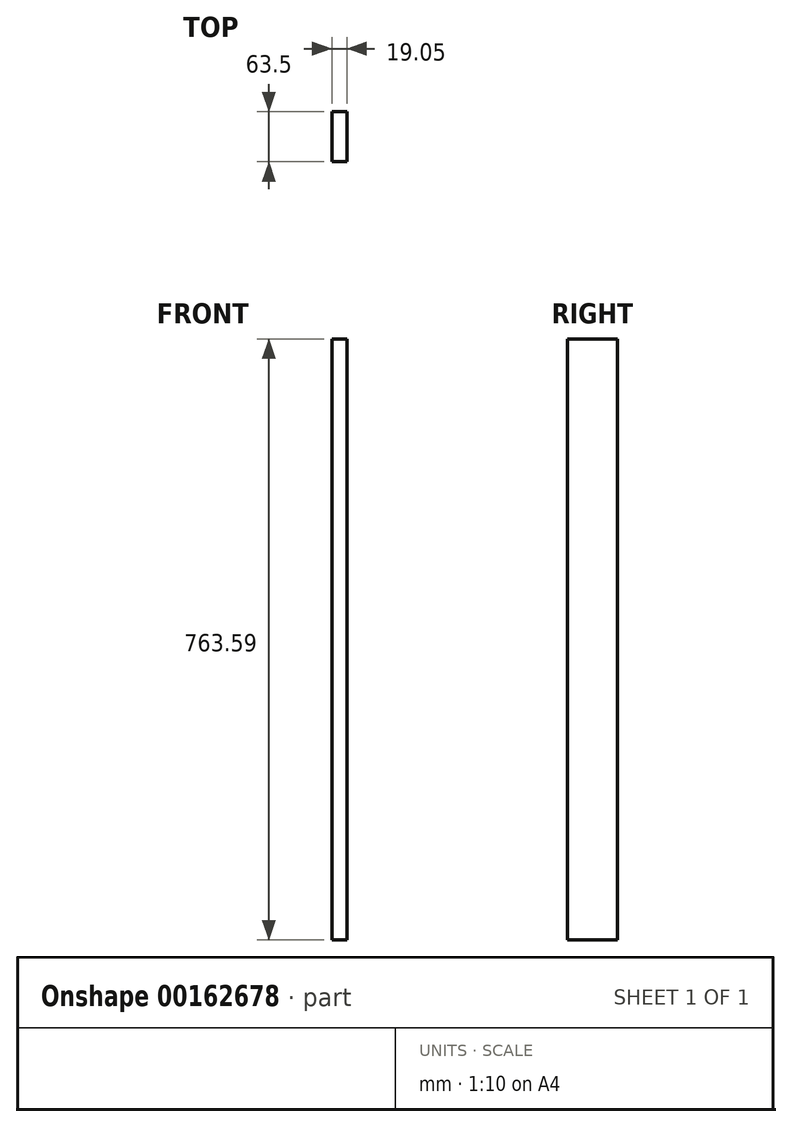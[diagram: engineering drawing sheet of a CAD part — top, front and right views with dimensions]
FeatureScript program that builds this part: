
annotation { "Feature Type Name" : "Feature", "Feature Type Description" : "" }
export const myFeature = defineFeature(function(context is Context, id is Id, definition is map)
    precondition{}
    {
        {
            var Q0;
            Q0=qCreatedBy(makeId("Right.planeOp"),FACE);
            var sketch = newSketch(context, id + "F0", { "sketchPlane" : qUnion([Q0])});
            skLineSegment(sketch, "E0.bottom", {"start": v(-41.08, 584.75) * mm, "end": v(22.42, 584.75) * mm});
            skLineSegment(sketch, "E0.top", {"start": v(-41.08, -178.84) * mm, "end": v(22.42, -178.84) * mm});
            skLineSegment(sketch, "E0.left", {"start": v(-41.08, 584.75) * mm, "end": v(-41.08, -178.84) * mm});
            skLineSegment(sketch, "E0.right", {"start": v(22.42, 584.75) * mm, "end": v(22.42, -178.84) * mm});
            skSolve(sketch);
        }
        {
            var Q0;
            Q0 = qSketchRegion(id + "F0", true);
            extrude(context, id + "F1", {"entities" : qUnion([Q0]), "depth" : 19.05 * mm});
        }
    });
